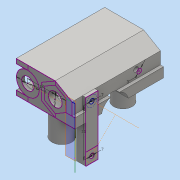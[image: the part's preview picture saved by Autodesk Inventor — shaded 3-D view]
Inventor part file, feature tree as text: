
AUTODESK INVENTOR PART (.ipt)
format: ipt  version: 2016 (Build 200138000, 138)  size: 243,200 bytes
history: native  units: mm
features: extrude x9, sketch x5, plane x1
ambient origin geometry x8: Origin, YZ Plane, XZ Plane, XY Plane, X Axis, Y Axis, Z Axis, Center Point
bodies: Solid1 (feature_tree)
feature tree (15):
  sketch  "Sketch1"  dims[d0=3.0mm d1=3.0mm]
  extrude  "Extrusion1"  Depth=3.0mm
  plane  "Work Plane6"
  sketch  "Sketch2"  dims[d3=31.0mm d6=7.0mm]
  extrude  "Extrusion6"  Depth=7.0mm
  extrude  "Extrusion5"  Depth=6.0mm TaperAngle=0.0deg
  sketch  "Sketch6"  dims[d7=7.0mm d9=6.0mm d10=0.0mm]
  extrude  "Extrusion8"  Depth=18.0mm
  extrude  "Extrusion9"  Depth=2.0mm
  extrude  "Extrusion10"  [1 undecoded]
  extrude  "Extrusion11"  Depth=2.0mm TaperAngle=0.0deg
  extrude  "Extrusion12"  Depth=5.0mm TaperAngle=0.0deg
  extrude  "Extrusion13"  Depth=2.0mm
  sketch  "Sketch7"  dims[d11=7.0mm d12=18.0mm]
  sketch  "Sketch8"  dims[d13=15.0mm d16=9.0mm d26=-15.0mm d27=58.0mm d28=0.0mm d29=5.0mm d30=0.0mm d51=18.0mm d52=20.0mm d53=20.0mm d54=8.0mm d55=8.0mm d56=15.0mm d57=0.0mm d58=15.0mm d59=0.0mm d60=2.068392mm d61=2.52468mm d62=15.0mm d63=0.0mm d64=3.0mm d65=15.0mm d66=0.0mm d67=15.0mm d68=2.0mm d69=0.0mm d70=8.0mm d71=2.0mm d72=0.0mm]
note: 1 required parameter value undecoded (feature->parameter linkage not recoverable at this tier; creation-order binding heuristic only, values carry confidence <= 0.55)
